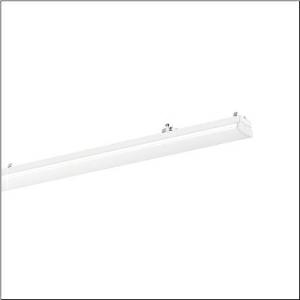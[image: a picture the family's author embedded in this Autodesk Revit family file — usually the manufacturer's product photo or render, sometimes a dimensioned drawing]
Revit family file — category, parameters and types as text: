
# Revit family: licross_r__11_recessed_opal_mo_51tl1ddv495g_cbeb
name_source: partatom
category: Lighting Fixtures
units: mm (PartAtom-declared; Revit-internal decimal feet)

## family parameters
Cut with Voids When Loaded = No
Host = Face
Light Source = No
Part Type = Normal
Room Calculation Point = No
Round Connector Dimension = Use Diameter
Shared = No

## types (1)
- --- (1 x LED, 9500 lm, 52.6 W, 4000K)
    Apparent Load = 53 VA
    CIE Flux Codes = 44 73 91 87 100
    Color Rendering = 80
    Color Temperature = 4000K
    Default Elevation = 1800 mm
    Description = Licross® 11 recessed opal MO, luminaire insert, of sheet steel, coil coated, white, length: 2.250mm, width: 76mm, height: 87mm, LED rated luminous flux: 9.500lm, light colour: 840, control gear: DALI 2, with plug, 5-pole, with phase selection, mains connection: 220..240V, AC, 50/60Hz, rated input power: 53W, halogen-free wiring, primary optical cover: cover, of PMMA, light emission: direct with ceiling illumination distribution, primary light characteristic: symmetric, protection rating (complete): IP40, insulation class (complete): insulation class I (protective earthing), certification: CE, ENEC, VDE, UKCA, protection symbol: D if used in an environment without relevant dust loads with corresponding accessories, impact resistance: IK06, permissible ambient temperature for indoor applications: -25..+40°C, corresponds to IFS (International Featured Standards) requirements for safety and quality in the food industry, reducing of maximum allowable ambient temperature of 5°C with ceiling mounting, LABS conformity tested according to VDMA 24364:2018-05, packaging unit: 1 piece
    Height = 83 mm
    Lamp = 1 x LED
    Lamp Light Flux = 9500 lm
    Lamp Power = 52.6 W
    Lamp count = 1
    Length = 2250 mm
    Luminous efficacy = 181 lm/W
    Manufacturer = Siteco
    ModVariant = No
    Model = 51TL1DDV495G
    Mounting Place = Ceiling
    Mounting Type = Pendant
    Number of Poles = 1
    OnlyDefault = Yes
    Power Factor = 1
    Product Name = Licross® 11 recessed opal MO
    Product group = luminaire insert
    ProductGroupID = 902
    Protection Class = Protection class I
    Protection Degree = IP 40
    RLX_Detail_Level = 1
    RLX_Emergency_Light_Flux = 0 lm
    RLX_Emergency_Type = 0
    RLX_Emergency_Type_DB = No
    RlxData = <blob elided: 26561 chars, md5=6ed1caaf>
    Socket = socket
    Standby Power = 0 W
    System Light Flux = 9500 lm
    System Power = 53 W
    Type Comments = factory setting: luminous flux: 100 % | dim-lin: 254 | 239 mA
    Type Image = l_1313666.jpg
    URL = http://relux.com
    VarID = @adj_076512
    Voltage = 0 V
    Weight = 0.00 kg
    Width = 76 mm

## geometry (parser evidence)
native form markers: Blend x4, Sweep x12
no freeform markers — native parametric forms only
